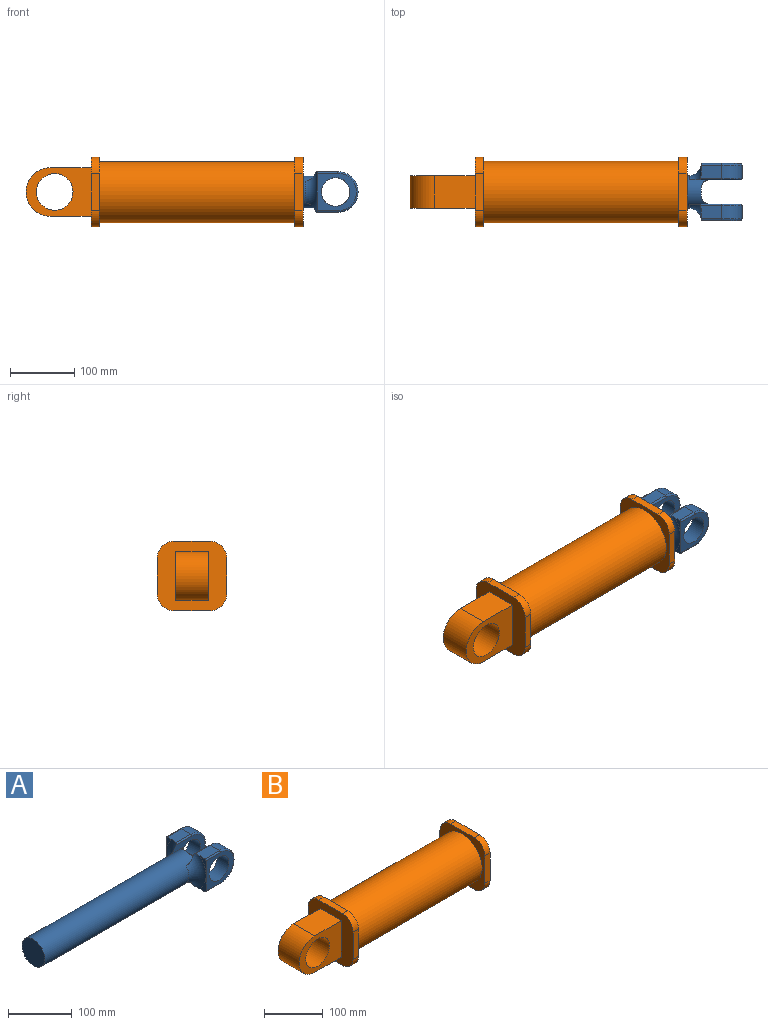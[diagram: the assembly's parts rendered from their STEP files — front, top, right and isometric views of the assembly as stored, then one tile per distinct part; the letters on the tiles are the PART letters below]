
ASSEMBLY  parts=2 mates=1
PART A: 39 faces, bbox 408x127.6x108 mm
  f0: plane 31.75x13.34mm, normal (-1,0,0), area 130.1mm2, adj f12,f13,f26,f32
  f1: plane 31.75x13.34mm, normal (-1,0,0), area 130.1mm2, adj f7,f8,f23,f31
  f2: plane 50.8x16.11mm, normal (1,0,0), area 691.1mm2, adj f3,f33,f34,f35,f36,f37,f38
  f3: cylinder r=25.4mm len=352.43mm, axis (-1,0,0), area 53002.4mm2, adj f2,f4,f6,f11,f31,f32,f33,f35
  f4: plane 50.8x50.8mm, normal (-1,0,0), area 2026.8mm2, adj f3
  f5: plane 31.75x13.34mm, normal (-1,0,0), area 130.1mm2, adj f8,f9,f22,f31
  f6: plane 82.15x60.56mm, normal (0,1,0), area 1541.9mm2, adj f3,f16,f19,f20,f21,f31,f36,f38
  f7: plane 33.31x20.9mm, normal (0,0,1), area 648.4mm2, adj f1,f18,f19,f23,f31
  f8: plane 60.96x58.42mm, normal (0,-1,0), area 1643.3mm2, adj f1,f5,f16,f22,f23,f24
  f9: plane 33.31x20.9mm, normal (0,0,-1), area 648.4mm2, adj f5,f18,f20,f22,f31
  f10: plane 33.31x20.9mm, normal (0,0,1), area 648.4mm2, adj f14,f17,f25,f29,f32
  f11: plane 82.15x60.56mm, normal (0,-1,0), area 1541.9mm2, adj f3,f15,f28,f29,f30,f32,f33,f35
  f12: plane 33.31x20.9mm, normal (0,0,-1), area 648.4mm2, adj f0,f17,f26,f28,f32
  f13: plane 60.96x58.42mm, normal (0,1,0), area 1643.3mm2, adj f0,f14,f15,f25,f26,f27
  f14: plane 31.75x13.34mm, normal (-1,0,0), area 130.1mm2, adj f10,f13,f25,f32
  f15: cylinder r=22.23mm len=44.45mm, axis (0,-1,0), area 3547mm2, adj f11,f13,f34
  f16: cylinder r=22.23mm len=44.45mm, axis (0,-1,0), area 3547mm2, adj f6,f8,f37
  f17: cylinder r=31.75mm len=63.5mm, axis (0,1,0), area 2026.8mm2, adj f10,f12,f27,f30
  f18: cylinder r=31.75mm len=63.5mm, axis (0,-1,0), area 2026.8mm2, adj f7,f9,f21,f24
  f19: cylinder r=2.54mm len=34.33mm, axis (1,0,0), area 133.8mm2, adj f6,f7,f21,f31
  f20: cylinder r=2.54mm len=34.33mm, axis (-1,0,0), area 133.8mm2, adj f6,f9,f21,f31
  f21: torus R=29.21mm, axis (0,1,0), area 386.4mm2, adj f6,f18,f19,f20
  f22: cylinder r=2.54mm len=31.75mm, axis (1,0,0), area 126.7mm2, adj f5,f8,f9,f24
  f23: cylinder r=2.54mm len=31.75mm, axis (-1,0,0), area 126.7mm2, adj f1,f7,f8,f24
  f24: torus R=29.21mm, axis (0,1,0), area 386.4mm2, adj f8,f18,f22,f23
  f25: cylinder r=2.54mm len=31.75mm, axis (1,0,0), area 126.7mm2, adj f10,f13,f14,f27
  f26: cylinder r=2.54mm len=31.75mm, axis (-1,0,0), area 126.7mm2, adj f0,f12,f13,f27
  f27: torus R=29.21mm, axis (0,1,0), area 386.4mm2, adj f13,f17,f25,f26
  f28: cylinder r=2.54mm len=34.33mm, axis (1,0,0), area 133.8mm2, adj f11,f12,f30,f32
  f29: cylinder r=2.54mm len=34.33mm, axis (-1,0,0), area 133.8mm2, adj f10,f11,f30,f32
  f30: torus R=29.21mm, axis (0,1,0), area 386.4mm2, adj f11,f17,f28,f29
  f31: torus R=44.45mm, axis (1,0,0), area 1720.1mm2, adj f1,f3,f5,f6,f7,f9,f19,f20
  f32: torus R=44.45mm, axis (1,0,0), area 1720.1mm2, adj f0,f3,f10,f11,f12,f14,f28,f29
  f33: cylinder r=12.7mm len=12.7mm, axis (0,0,-1), area 96mm2, adj f2,f3,f11,f34
  f34: bspline ~34.53x13.65mm, area 483.7mm2, adj f2,f15,f33,f35
  f35: cylinder r=12.7mm len=12.7mm, axis (0,0,-1), area 96mm2, adj f2,f3,f11,f34
  f36: cylinder r=12.7mm len=12.7mm, axis (0,0,1), area 96mm2, adj f2,f3,f6,f37
  f37: bspline ~34.53x13.65mm, area 483.7mm2, adj f2,f16,f36,f38
  f38: cylinder r=12.7mm len=12.7mm, axis (0,0,1), area 96mm2, adj f2,f3,f6,f37
PART B: 31 faces, bbox 431.8x108x108 mm
  f0: plane 107.95x107.95mm, normal (-1,0,0), area 7228.4mm2, adj f7,f8,f9,f10,f11,f12,f13,f14
  f1: plane 76.2x76.2mm, normal (1,0,0), area 4560.4mm2, adj f2
  f2: cylinder r=38.1mm len=304.8mm, axis (-1,0,0), area 72965.9mm2, adj f1,f3
  f3: plane 76.2x76.2mm, normal (-1,0,0), area 2533.5mm2, adj f2,f4
  f4: cylinder r=25.4mm len=50.8mm, axis (1,0,0), area 2026.8mm2, adj f3,f16
  f5: cylinder r=47.62mm len=304.8mm, axis (-1,0,0), area 91207.3mm2, adj f6,f15
  f6: plane 107.95x107.95mm, normal (1,0,0), area 3973.8mm2, adj f5,f7,f8,f9,f10,f11,f12,f13
  f7: plane 57.15x12.7mm, normal (0,0,-1), area 725.8mm2, adj f0,f6,f13,f14
  f8: plane 57.15x12.7mm, normal (0,1,0), area 725.8mm2, adj f0,f6,f12,f13
  f9: plane 57.15x12.7mm, normal (0,0,1), area 725.8mm2, adj f0,f6,f11,f12
  f10: plane 57.15x12.7mm, normal (0,-1,0), area 725.8mm2, adj f0,f6,f11,f14
  f11: cylinder r=25.4mm len=25.4mm, axis (-1,0,0), area 506.7mm2, adj f0,f6,f9,f10
  f12: cylinder r=25.4mm len=25.4mm, axis (1,0,0), area 506.7mm2, adj f0,f6,f8,f9
  f13: cylinder r=25.4mm len=25.4mm, axis (-1,0,0), area 506.7mm2, adj f0,f6,f7,f8
  f14: cylinder r=25.4mm len=25.4mm, axis (1,0,0), area 506.7mm2, adj f0,f6,f7,f10
  f15: plane 107.95x107.95mm, normal (-1,0,0), area 3973.8mm2, adj f5,f17,f18,f19,f20,f21,f22,f23
  f16: plane 107.95x107.95mm, normal (1,0,0), area 9072.6mm2, adj f4,f17,f18,f19,f20,f21,f22,f23
  f17: plane 57.15x12.7mm, normal (0,0,-1), area 725.8mm2, adj f15,f16,f23,f24
  f18: plane 57.15x12.7mm, normal (0,-1,0), area 725.8mm2, adj f15,f16,f22,f23
  f19: plane 57.15x12.7mm, normal (0,0,1), area 725.8mm2, adj f15,f16,f21,f22
  f20: plane 57.15x12.7mm, normal (0,1,0), area 725.8mm2, adj f15,f16,f21,f24
  f21: cylinder r=25.4mm len=25.4mm, axis (1,0,0), area 506.7mm2, adj f15,f16,f19,f20
  f22: cylinder r=25.4mm len=25.4mm, axis (-1,0,0), area 506.7mm2, adj f15,f16,f18,f19
  f23: cylinder r=25.4mm len=25.4mm, axis (1,0,0), area 506.7mm2, adj f15,f16,f17,f18
  f24: cylinder r=25.4mm len=25.4mm, axis (-1,0,0), area 506.7mm2, adj f15,f16,f17,f20
  f25: plane 101.6x76.2mm, normal (0,-1,0), area 4553.7mm2, adj f0,f26,f28,f29,f30
  f26: plane 63.5x50.8mm, normal (0,0,1), area 3225.8mm2, adj f0,f25,f27,f30
  f27: plane 101.6x76.2mm, normal (0,1,0), area 4553.7mm2, adj f0,f26,f28,f29,f30
  f28: plane 63.5x50.8mm, normal (0,0,-1), area 3225.8mm2, adj f0,f25,f27,f30
  f29: cylinder r=28.57mm len=57.15mm, axis (0,-1,0), area 9120.7mm2, adj f25,f27
  f30: cylinder r=38.1mm len=76.2mm, axis (0,1,0), area 6080.5mm2, adj f25,f26,f27,f28
PLACE A t=(137.9,2.84,-98.98)mm
PLACE B t=(150.6,2.84,-98.98)mm fixed
MATE slider B.f5 <-> A.f3  axis (-1,0,0) through (-1.8,2.84,-98.98)mm
